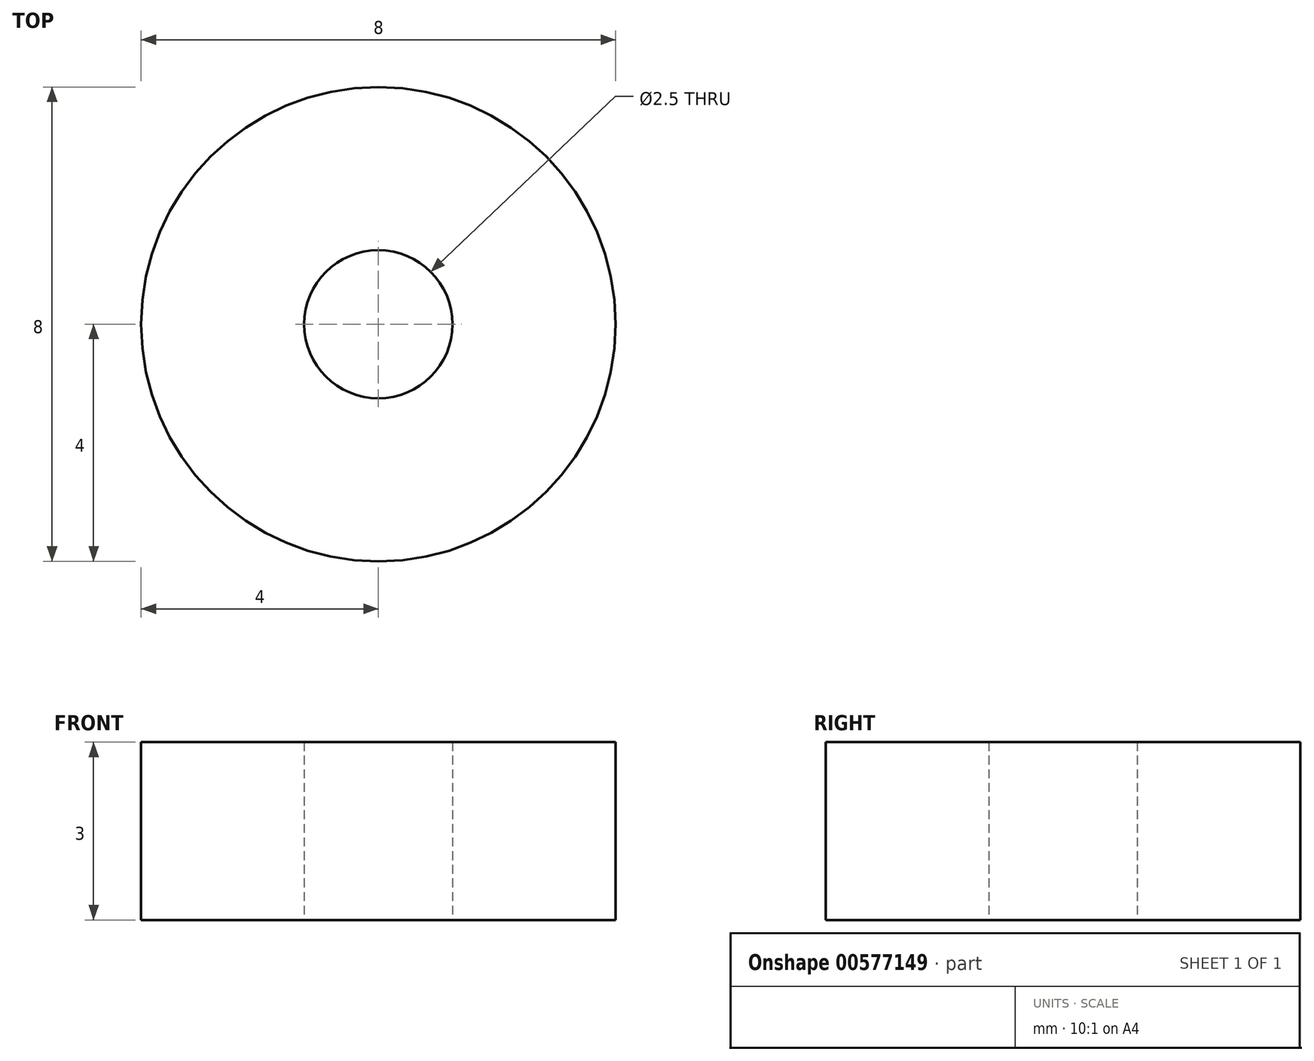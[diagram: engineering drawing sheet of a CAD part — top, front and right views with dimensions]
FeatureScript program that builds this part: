
annotation { "Feature Type Name" : "Feature", "Feature Type Description" : "" }
export const myFeature = defineFeature(function(context is Context, id is Id, definition is map)
    precondition{}
    {
        {
            var Q0;
            Q0=qCreatedBy(makeId("Top.planeOp"),FACE);
            var sketch = newSketch(context, id + "F0", { "sketchPlane" : qUnion([Q0])});
            skCircle(sketch, "E0", {"center": v(0, 0) * mm, "radius": 1.25 * mm});
            skCircle(sketch, "E1", {"center": v(0, 0) * mm, "radius": 4 * mm});
            skSolve(sketch);
        }
        {
            var Q0;
            Q0=qSketchRegion(id+"F0",true);
            extrude(context, id + "F1", {"entities" : qUnion([Q0]), "depth" : 3 * mm});
        }
    });
